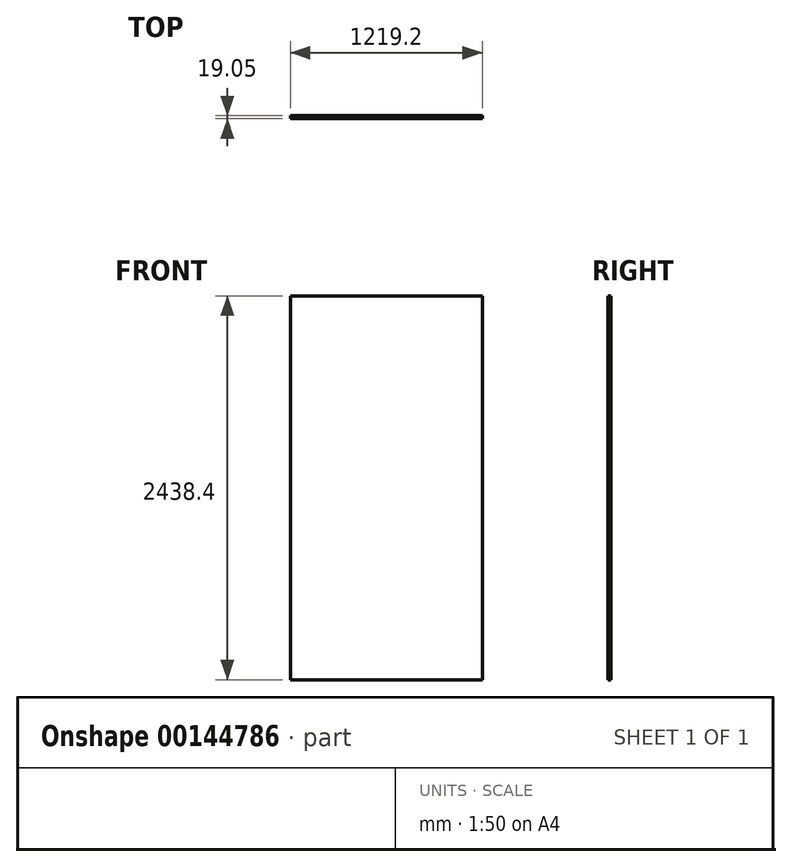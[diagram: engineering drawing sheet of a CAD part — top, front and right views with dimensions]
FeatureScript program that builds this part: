
annotation { "Feature Type Name" : "Feature", "Feature Type Description" : "" }
export const myFeature = defineFeature(function(context is Context, id is Id, definition is map)
    precondition{}
    {
        {
            var Q0;
            Q0=qCreatedBy(makeId("Front.planeOp"),FACE);
            var sketch = newSketch(context, id + "F0", { "sketchPlane" : qUnion([Q0])});
            skLineSegment(sketch, "E0.bottom", {"start": v(0, 0) * mm, "end": v(1219.2, 0) * mm});
            skLineSegment(sketch, "E0.top", {"start": v(0, 2438.4) * mm, "end": v(1219.2, 2438.4) * mm});
            skLineSegment(sketch, "E0.left", {"start": v(0, 0) * mm, "end": v(0, 2438.4) * mm});
            skLineSegment(sketch, "E0.right", {"start": v(1219.2, 0) * mm, "end": v(1219.2, 2438.4) * mm});
            skSolve(sketch);
        }
        {
            var Q0;
            Q0=makeQuery(id+"F0.imprint","IMPRINT",FACE,{"disambiguationData":[TD([[makeQuery(id+"F0.imprint","IMPRINT",EDGE,{"derivedFrom":sQuery(id+"F0.wireOp",EDGE,"E0.bottom")}),1.0]])]});
            var Q1;
            Q1=makeQuery(id+"F0.imprint","IMPRINT",FACE,{"disambiguationData":[TD([[makeQuery(id+"F0.imprint","IMPRINT",EDGE,{"derivedFrom":sQuery(id+"F0.wireOp",EDGE,"E0.bottom")}),1.0]])]});
            extrude(context, id + "F1", {"entities" : qUnion([Q0, Q1]), "depth" : 19.05 * mm});
        }
    });
